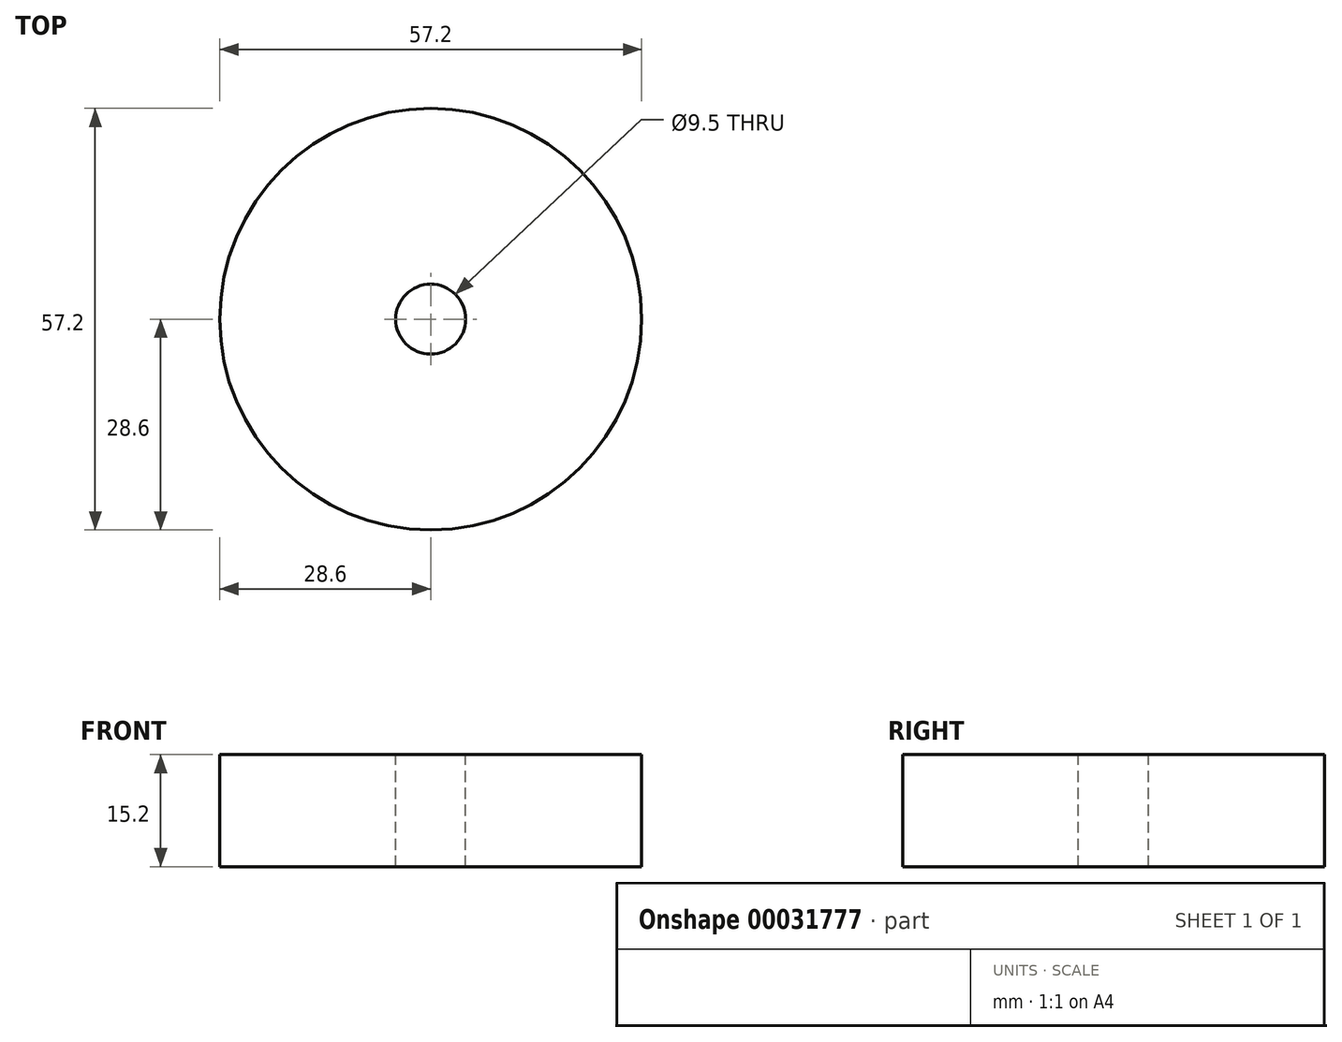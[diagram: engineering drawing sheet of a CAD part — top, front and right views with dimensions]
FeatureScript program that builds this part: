
annotation { "Feature Type Name" : "Feature", "Feature Type Description" : "" }
export const myFeature = defineFeature(function(context is Context, id is Id, definition is map)
    precondition{}
    {
        {
            var Q0;
            Q0=qCreatedBy(makeId("Top.planeOp"),FACE);
            var sketch = newSketch(context, id + "F0", { "sketchPlane" : qUnion([Q0])});
            skCircle(sketch, "E0", {"center": v(0, 0) * mm, "radius": 28.6 * mm});
            skSolve(sketch);
        }
        {
            var Q0;
            Q0=makeQuery(id+"F0.imprint","IMPRINT",FACE,{"disambiguationData":[TD([[makeQuery(id+"F0.imprint","IMPRINT",EDGE,{"derivedFrom":sQuery(id+"F0.wireOp",EDGE,"E0")}),1.0]])]});
            extrude(context, id + "F1", {"entities" : qUnion([Q0]), "depth" : 15.2 * mm});
        }
        {
            var Q0;
            Q0=makeQuery(id+"FAwBjHM2YBxepDU_1.boolean.opBoolean","MERGE",FACE,{"derivedFrom":[makeQuery(id+"F1.opExtrude","CAP_FACE",FACE,{"disambiguationData":[OSD([sQuery(id+"F0.wireOp",EDGE,"E0")])],"isStart":false}),makeQuery(id+"FAwBjHM2YBxepDU_1.opExtrude","CAP_FACE",FACE,{"disambiguationData":[OSD([sQuery(id+"FGgvQecDUPhJ594_1.wireOp",EDGE,"b37fd889-66c8-4e0c-90b2-a7e21b4c1b01"),sQuery(id+"FGgvQecDUPhJ594_1.wireOp",EDGE,"0cdc9503-3e7d-431a-bc8f-75cffd5b71a0"),sQuery(id+"FGgvQecDUPhJ594_1.wireOp",EDGE,"40c0f8ea-ffa2-4680-836d-abe5fe890ce1"),sQuery(id+"FGgvQecDUPhJ594_1.wireOp",EDGE,"f22514f2-767f-4c63-8c46-58f86d0df8e9"),sQuery(id+"FGgvQecDUPhJ594_1.wireOp",EDGE,"3f67fe07-063e-46eb-8cae-f2ad7882b61c0.MirrorCS"),sQuery(id+"FGgvQecDUPhJ594_1.wireOp",EDGE,"990837da-8a0f-420d-a47e-854dad9813460.MirrorCS"),sQuery(id+"FGgvQecDUPhJ594_1.wireOp",EDGE,"ef43964c-366b-402e-9953-c09aedb6aeb20.MirrorCS"),sQuery(id+"FGgvQecDUPhJ594_1.wireOp",EDGE,"235a6d0c-f9d4-4cde-af29-7d0831b8fd1a0.MirrorCS"),sQuery(id+"FGgvQecDUPhJ594_1.wireOp",EDGE,"01a041d1-0760-40e8-8462-8d657b9ceef40.MirrorCS"),sQuery(id+"FGgvQecDUPhJ594_1.wireOp",EDGE,"b9e8de0c-705d-4e03-9c48-207347edb41a0.MirrorCS"),sQuery(id+"FGgvQecDUPhJ594_1.wireOp",EDGE,"8f080f48-3f1a-4d8e-b90b-6224b0bb5c380.MirrorCS"),sQuery(id+"FGgvQecDUPhJ594_1.wireOp",EDGE,"f75e8129-24c5-4716-bdcc-67a85d64204e0.MirrorCS"),sQuery(id+"FGgvQecDUPhJ594_1.wireOp",EDGE,"512c65d0-c898-4b63-8c1d-3d0c811e248c0.MirrorCS")])],"isStart":false})]});
            var sketch = newSketch(context, id + "F2", { "sketchPlane" : qUnion([Q0])});
            skCircle(sketch, "E1", {"center": v(0, 0) * mm, "radius": 4.75 * mm});
            skSolve(sketch);
        }
        {
            var Q0;
            Q0 = qSketchRegion(id + "F2", true);
            extrude(context, id + "F3", {"entities" : qUnion([Q0]), "operationType" : NewBodyOperationType.REMOVE, "oppositeDirection" : true, "depth" : 25 * mm});
        }
        {
            var Q0;
            Q0=makeQuery(id+"F1.opExtrude","CAP_FACE",FACE,{"disambiguationData":[OSD([sQuery(id+"F0.wireOp",EDGE,"E0")])],"isStart":false});
            cPlane(context, id + "F4", {"entities" : qUnion([Q0]), "cplaneType" : CPlaneType.OFFSET, "offset" : 75 * mm, "width" : 150 * mm, "height" : 150 * mm});
        }
    });
